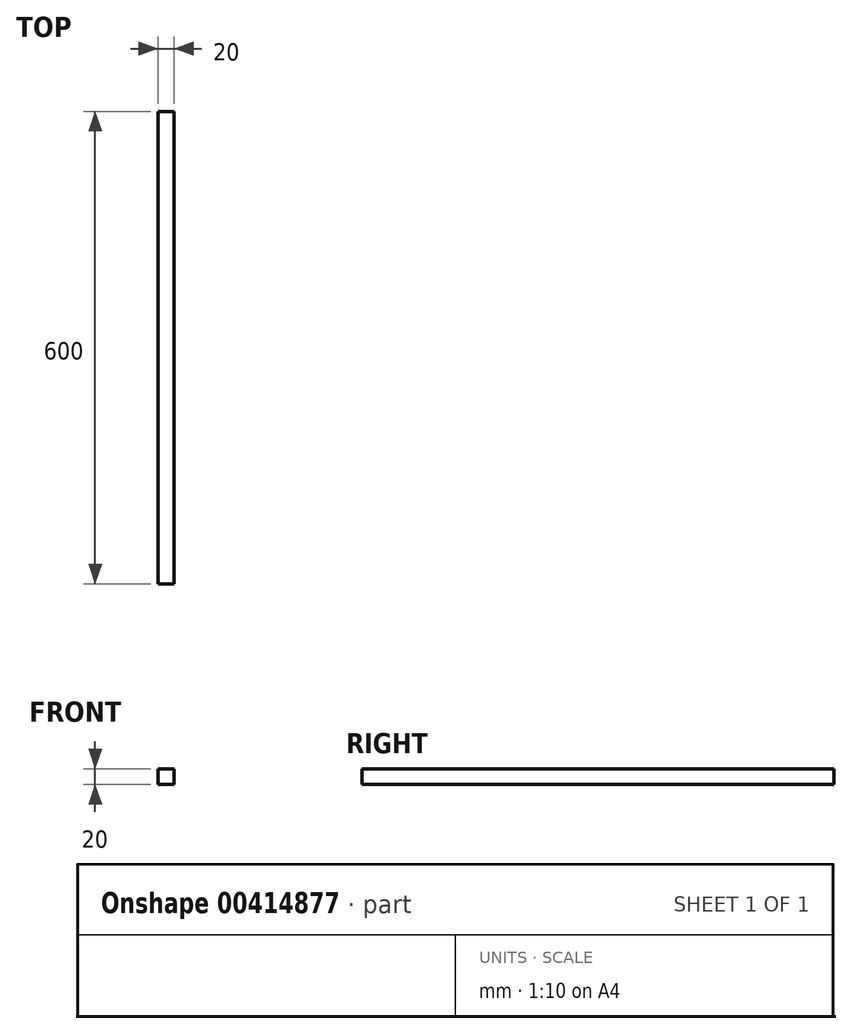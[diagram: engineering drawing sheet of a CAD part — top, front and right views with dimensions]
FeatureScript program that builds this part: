
annotation { "Feature Type Name" : "Feature", "Feature Type Description" : "" }
export const myFeature = defineFeature(function(context is Context, id is Id, definition is map)
    precondition{}
    {
        {
            var Q0;
            Q0=qCreatedBy(makeId("Front.planeOp"),FACE);
            var sketch = newSketch(context, id + "F0", { "sketchPlane" : qUnion([Q0])});
            skLineSegment(sketch, "E0.bottom", {"start": v(-10, 20) * mm, "end": v(10, 20) * mm});
            skLineSegment(sketch, "E0.top", {"start": v(-10, 0) * mm, "end": v(10, 0) * mm});
            skLineSegment(sketch, "E0.left", {"start": v(-10, 20) * mm, "end": v(-10, 0) * mm});
            skLineSegment(sketch, "E0.right", {"start": v(10, 20) * mm, "end": v(10, 0) * mm});
            skSolve(sketch);
        }
        {
            var Q0;
            Q0=makeQuery(id+"F0.imprint","IMPRINT",FACE,{"disambiguationData":[TD([[makeQuery(id+"F0.imprint","IMPRINT",EDGE,{"derivedFrom":sQuery(id+"F0.wireOp",EDGE,"E0.bottom")}),-1.0]])]});
            extrude(context, id + "F1", {"entities" : qUnion([Q0]), "endBound" : BoundingType.SYMMETRIC, "depth" : 600 * mm});
        }
    });
